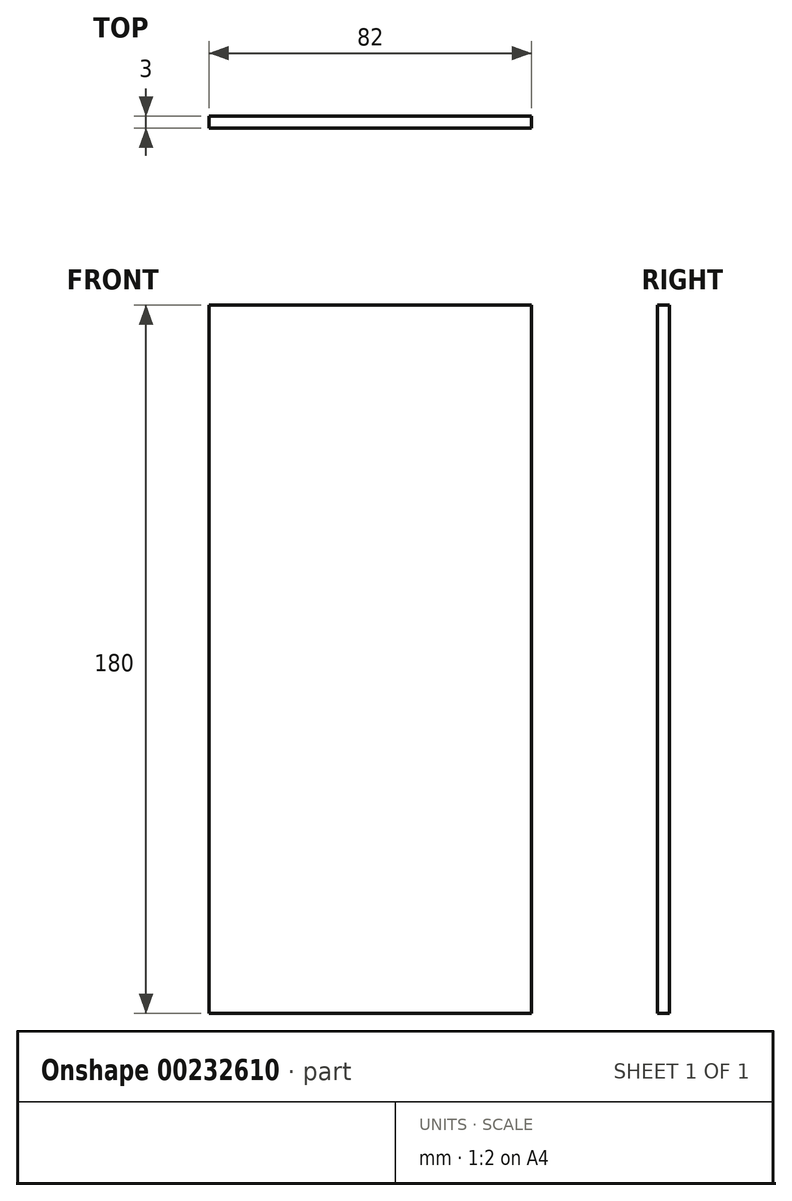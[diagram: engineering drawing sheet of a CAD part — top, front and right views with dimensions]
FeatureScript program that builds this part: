
annotation { "Feature Type Name" : "Feature", "Feature Type Description" : "" }
export const myFeature = defineFeature(function(context is Context, id is Id, definition is map)
    precondition{}
    {
        {
            var Q0;
            Q0=qCreatedBy(makeId("Front.planeOp"),FACE);
            var sketch = newSketch(context, id + "F0", { "sketchPlane" : qUnion([Q0])});
            skLineSegment(sketch, "E0.bottom", {"start": v(0, 0) * mm, "end": v(82, 0) * mm});
            skLineSegment(sketch, "E0.top", {"start": v(0, 180) * mm, "end": v(82, 180) * mm});
            skLineSegment(sketch, "E0.left", {"start": v(0, 0) * mm, "end": v(0, 180) * mm});
            skLineSegment(sketch, "E0.right", {"start": v(82, 0) * mm, "end": v(82, 180) * mm});
            skSolve(sketch);
        }
        {
            var Q0;
            Q0 = qSketchRegion(id + "F0", true);
            extrude(context, id + "F1", {"entities" : qUnion([Q0]), "depth" : 3 * mm});
        }
    });
